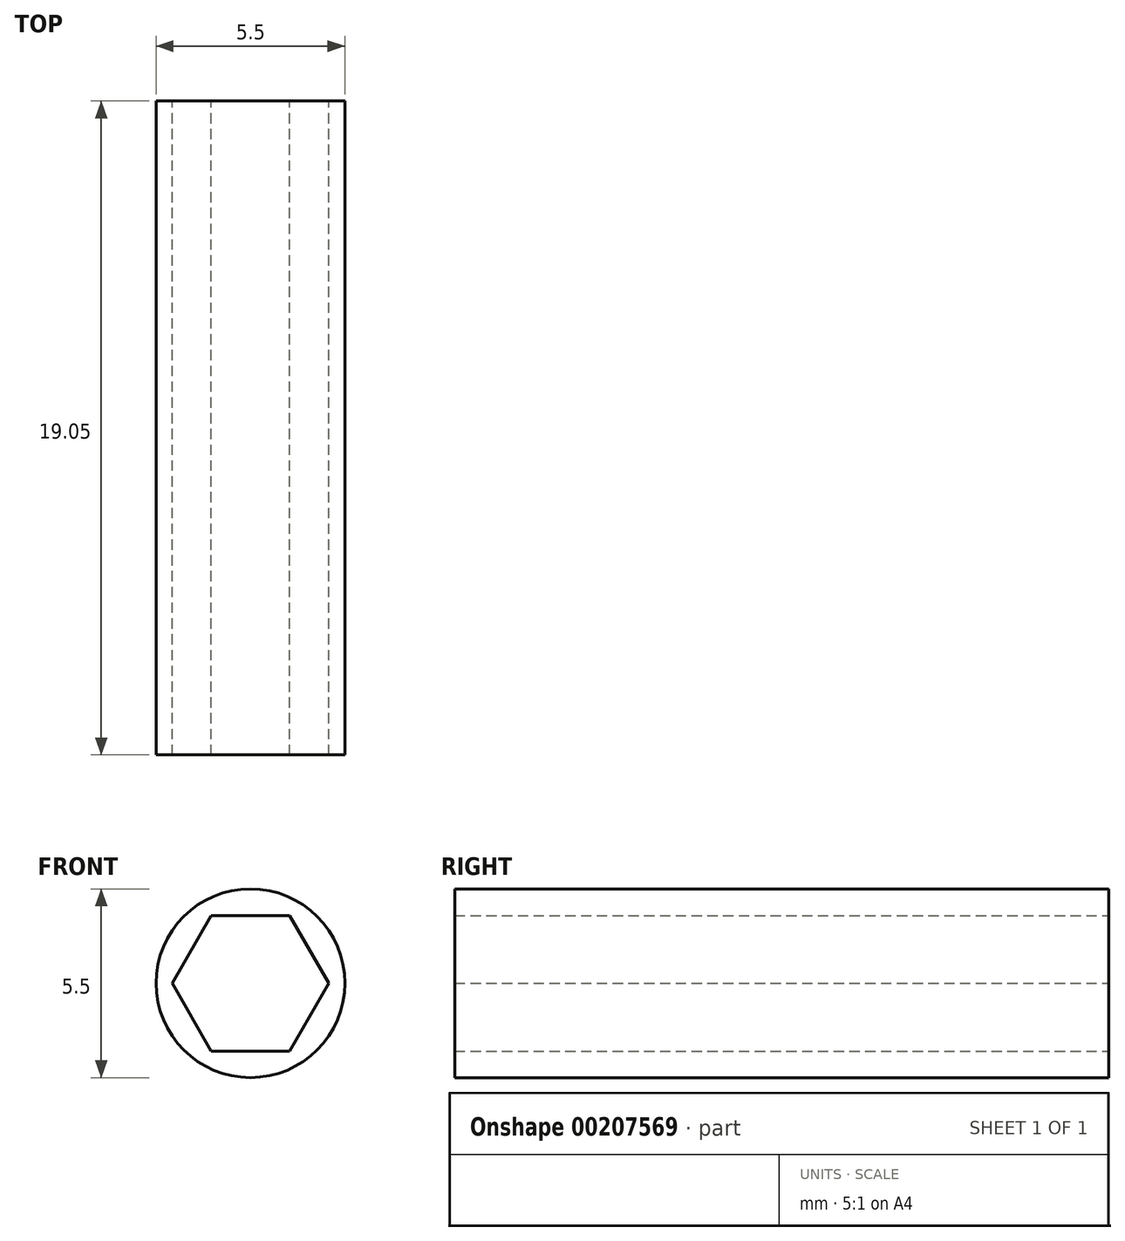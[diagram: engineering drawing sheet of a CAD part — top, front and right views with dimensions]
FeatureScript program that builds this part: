
annotation { "Feature Type Name" : "Feature", "Feature Type Description" : "" }
export const myFeature = defineFeature(function(context is Context, id is Id, definition is map)
    precondition{}
    {
        {
            var Q0;
            Q0=qCreatedBy(makeId("Front.planeOp"),FACE);
            var sketch = newSketch(context, id + "F0", { "sketchPlane" : qUnion([Q0])});
            skCircle(sketch, "E0.cCircle", {"center": v(0, 0) * mm, "radius": 1.98 * mm, "construction": true});
            skLineSegment(sketch, "E0.0", {"start": v(2.28, 0) * mm, "end": v(1.14, -1.98) * mm});
            skLineSegment(sketch, "E0.1", {"start": v(1.14, -1.98) * mm, "end": v(-1.14, -1.98) * mm});
            skLineSegment(sketch, "E0.2", {"start": v(-1.14, -1.98) * mm, "end": v(-2.28, 0) * mm});
            skLineSegment(sketch, "E0.3", {"start": v(-2.28, 0) * mm, "end": v(-1.14, 1.97) * mm});
            skLineSegment(sketch, "E0.4", {"start": v(-1.14, 1.98) * mm, "end": v(1.14, 1.98) * mm});
            skLineSegment(sketch, "E0.5", {"start": v(1.14, 1.97) * mm, "end": v(2.28, 0) * mm});
            skPoint(sketch, "E0.0.midPoint", {"position": v(1.71, -0.99) * mm});
            skLineSegment(sketch, "E1", {"start": v(0, 1.98) * mm, "end": v(0, -1.98) * mm, "construction": true});
            skCircle(sketch, "E2", {"center": v(0, 0) * mm, "radius": 2.75 * mm});
            skLineSegment(sketch, "E3", {"start": v(-2.28, 0) * mm, "end": v(2.28, 0) * mm, "construction": true});
            skSolve(sketch);
        }
        {
            var Q0;
            Q0=makeQuery(id+"F0.imprint","IMPRINT",FACE,{"disambiguationData":[TD([[makeQuery(id+"F0.imprint","IMPRINT",EDGE,{"derivedFrom":sQuery(id+"F0.wireOp",EDGE,"E0.0")}),1.0]])]});
            extrude(context, id + "F1", {"entities" : qUnion([Q0]), "depth" : 19.05 * mm});
        }
    });
